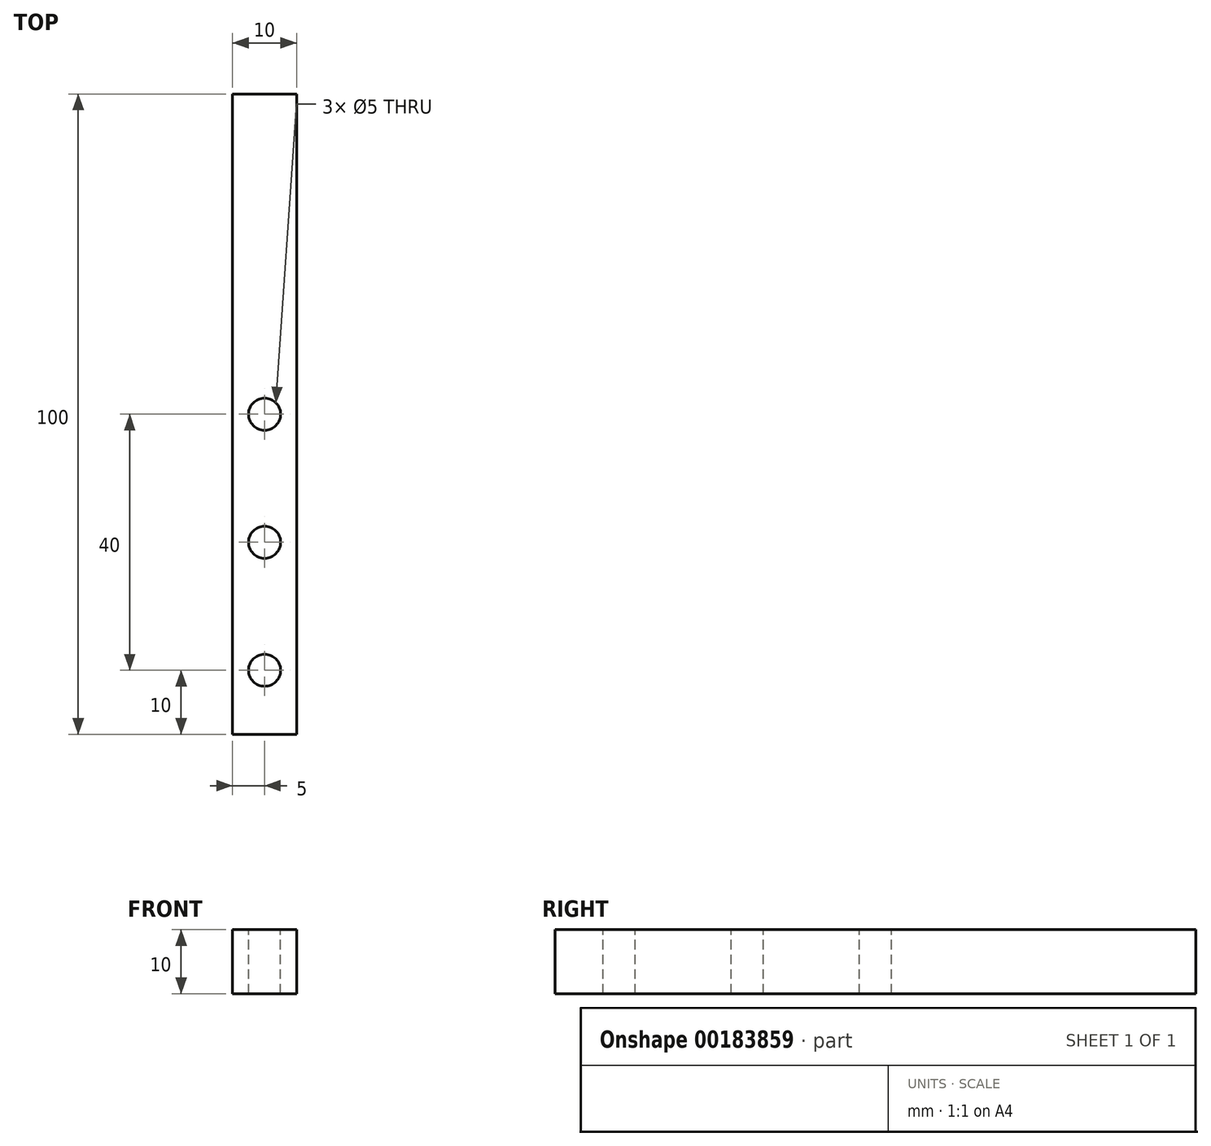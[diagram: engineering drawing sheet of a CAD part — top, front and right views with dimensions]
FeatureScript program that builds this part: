
annotation { "Feature Type Name" : "Feature", "Feature Type Description" : "" }
export const myFeature = defineFeature(function(context is Context, id is Id, definition is map)
    precondition{}
    {
        {
            var Q0;
            Q0=qCreatedBy(makeId("Top.planeOp"),FACE);
            var sketch = newSketch(context, id + "F0", { "sketchPlane" : qUnion([Q0])});
            skLineSegment(sketch, "E0.bottom", {"start": v(-5, 50) * mm, "end": v(5, 50) * mm});
            skLineSegment(sketch, "E0.top", {"start": v(-5, -50) * mm, "end": v(5, -50) * mm});
            skLineSegment(sketch, "E0.left", {"start": v(-5, 50) * mm, "end": v(-5, -50) * mm});
            skLineSegment(sketch, "E0.right", {"start": v(5, 50) * mm, "end": v(5, -50) * mm});
            skPoint(sketch, "E0.middle", {"position": v(0, 0) * mm});
            skSolve(sketch);
        }
        {
            var Q0;
            Q0 = qSketchRegion(id + "F0", true);
            extrude(context, id + "F1", {"entities" : qUnion([Q0]), "depth" : 10 * mm});
        }
        {
            var Q0;
            Q0=makeQuery(id+"F1.opExtrude","CAP_FACE",FACE,{"disambiguationData":[OSD([sQuery(id+"F0.wireOp",EDGE,"E0.bottom"),sQuery(id+"F0.wireOp",EDGE,"E0.top"),sQuery(id+"F0.wireOp",EDGE,"E0.left"),sQuery(id+"F0.wireOp",EDGE,"E0.right")])],"isStart":false});
            var sketch = newSketch(context, id + "F2", { "sketchPlane" : qUnion([Q0])});
            skCircle(sketch, "E1", {"center": v(0, 0) * mm, "radius": 2.5 * mm});
            skCircle(sketch, "E2.1.0.0", {"center": v(0, -20) * mm, "radius": 2.5 * mm});
            skCircle(sketch, "E2.2.0.0", {"center": v(0, -40) * mm, "radius": 2.5 * mm});
            skLineSegment(sketch, "E2.direction1", {"start": v(0, 0) * mm, "end": v(0, -20) * mm, "construction": true});
            skSolve(sketch);
        }
        {
            var Q0;
            Q0 = qSketchRegion(id + "F2", true);
            extrude(context, id + "F3", {"entities" : qUnion([Q0]), "operationType" : NewBodyOperationType.REMOVE, "endBound" : BoundingType.UP_TO_NEXT, "oppositeDirection" : true, "depth" : 25 * mm});
        }
    });
